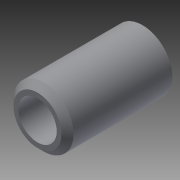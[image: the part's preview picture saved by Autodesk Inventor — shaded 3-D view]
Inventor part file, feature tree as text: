
AUTODESK INVENTOR PART (.ipt)
format: ipt  version: 2015 SP1 (Build 190203100, 203)  size: 88,064 bytes
history: native  units: in
note: dims shown in document units (in); Inventor stores cm internally (conversion verified against a paired STEP export)
features: extrude x1, chamfer x1, sketch x1
ambient origin geometry x8: Origin, YZ Plane, XZ Plane, XY Plane, X Axis, Y Axis, Z Axis, Center Point
bodies: Solid1 (feature_tree)
feature tree (3):
  extrude  "Extrusion1"  Depth=1.75in
  chamfer  "Chamfer1"  Distance=1.75in
  sketch  "Sketch1"  dims[d0=1.0in d2=0.6406in d3=1.75in d4=0.0in d5=0.1in d6=0.125in d7=45.0deg]
